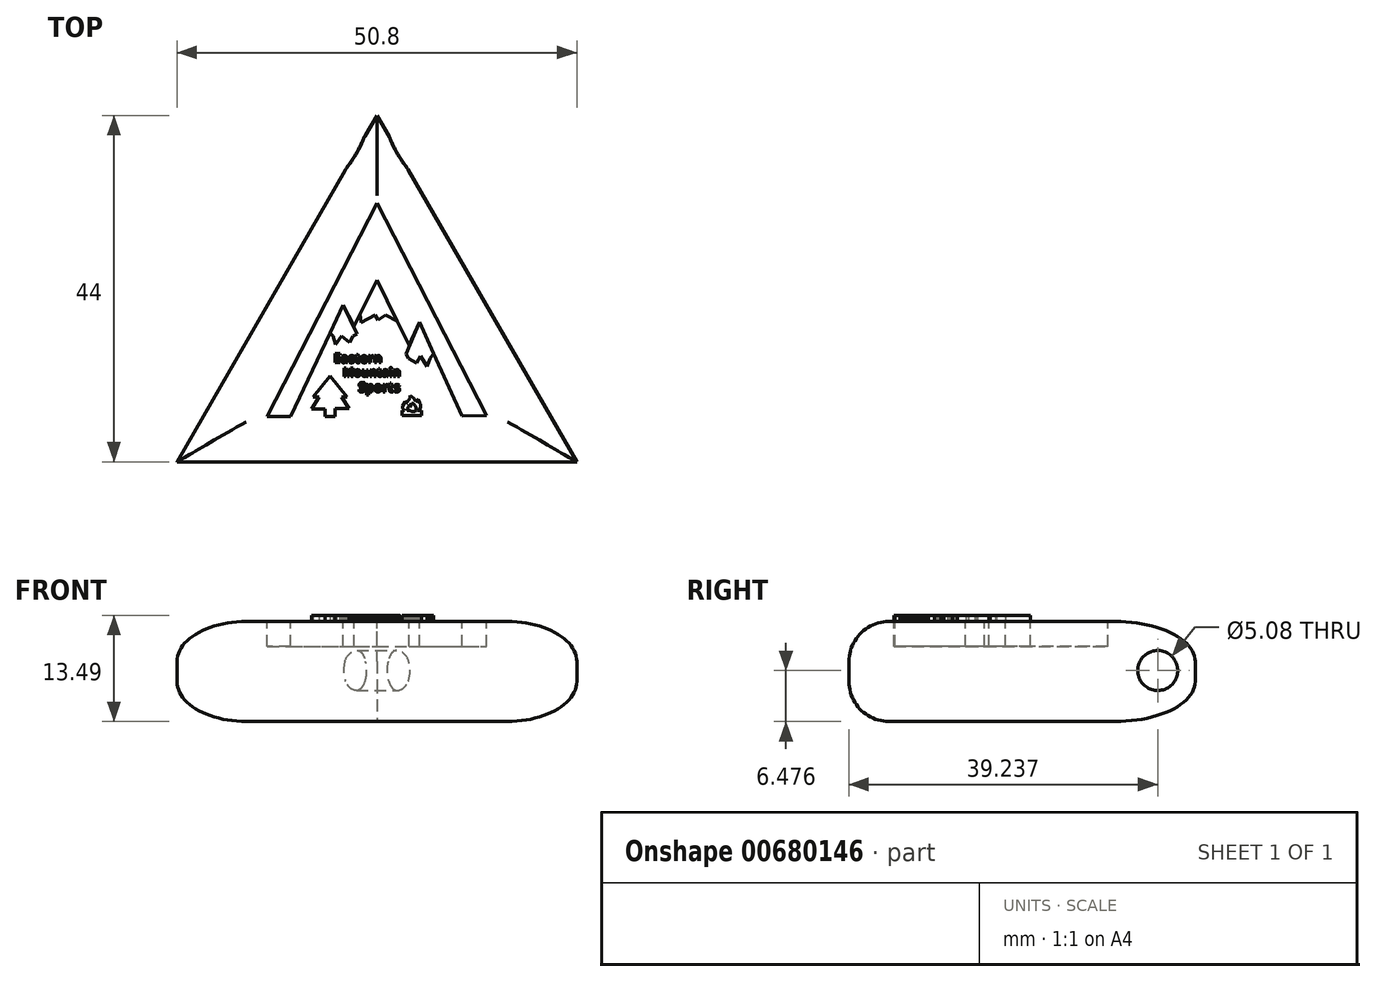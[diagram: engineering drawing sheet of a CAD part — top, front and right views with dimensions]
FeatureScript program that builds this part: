
annotation { "Feature Type Name" : "Feature", "Feature Type Description" : "" }
export const myFeature = defineFeature(function(context is Context, id is Id, definition is map)
    precondition{}
    {
        {
            var Q0;
            Q0=qCreatedBy(makeId("Top.planeOp"),FACE);
            var sketch = newSketch(context, id + "F0", { "sketchPlane" : qUnion([Q0])});
            skLineSegment(sketch, "E0", {"start": v(0, 54.4) * mm, "end": v(-25.4, 10.41) * mm});
            skLineSegment(sketch, "E1", {"start": v(-25.4, 10.41) * mm, "end": v(25.4, 10.41) * mm});
            skLineSegment(sketch, "E2", {"start": v(25.4, 10.41) * mm, "end": v(0, 54.4) * mm});
            skSolve(sketch);
        }
        {
            var Q0;
            Q0 = qSketchRegion(id + "F0", true);
            extrude(context, id + "F1", {"entities" : qUnion([Q0]), "depth" : 12.7 * mm, "offsetDistance" : 25.4 * mm});
        }
        {
            var Q0;
            Q0=makeQuery(id+"F1.opExtrude","CAP_EDGE",EDGE,{"disambiguationData":[OSD([sQuery(id+"F0.wireOp",EDGE,"E1")])],"isStart":false});
            var Q1;
            Q1=makeQuery(id+"F1.opExtrude","CAP_EDGE",EDGE,{"disambiguationData":[OSD([sQuery(id+"F0.wireOp",EDGE,"E0")])],"isStart":false});
            var Q2;
            Q2=makeQuery(id+"F1.opExtrude","CAP_EDGE",EDGE,{"disambiguationData":[OSD([sQuery(id+"F0.wireOp",EDGE,"E2")])],"isStart":false});
            var Q3;
            Q3=makeQuery(id+"F1.opExtrude","CAP_EDGE",EDGE,{"disambiguationData":[OSD([sQuery(id+"F0.wireOp",EDGE,"E1")])],"isStart":true});
            var Q4;
            Q4=makeQuery(id+"F1.opExtrude","CAP_EDGE",EDGE,{"disambiguationData":[OSD([sQuery(id+"F0.wireOp",EDGE,"E0")])],"isStart":true});
            var Q5;
            Q5=makeQuery(id+"F1.opExtrude","CAP_EDGE",EDGE,{"disambiguationData":[OSD([sQuery(id+"F0.wireOp",EDGE,"E2")])],"isStart":true});
            fillet(context, id + "F2", {"entities" : qUnion([Q0, Q1, Q2, Q3, Q4, Q5]), "radius" : 5.08 * mm, "tangentPropagation" : true, "allowEdgeOverflow" : false});
        }
        {
            var Q0;
            Q0=qCreatedBy(makeId("Right.planeOp"),FACE);
            var sketch = newSketch(context, id + "F3", { "sketchPlane" : qUnion([Q0])});
            skCircle(sketch, "E3", {"center": v(49.65, 6.48) * mm, "radius": 2.54 * mm});
            skSolve(sketch);
        }
        {
            var Q0;
            Q0 = qSketchRegion(id + "F3", true);
            extrude(context, id + "F4", {"entities" : qUnion([Q0]), "operationType" : NewBodyOperationType.REMOVE, "oppositeDirection" : true, "depth" : 25.4 * mm, "offsetDistance" : 25.4 * mm});
        }
        {
            var Q0;
            Q0 = qSketchRegion(id + "F3", true);
            extrude(context, id + "F5", {"entities" : qUnion([Q0]), "operationType" : NewBodyOperationType.REMOVE, "depth" : 25.4 * mm, "offsetDistance" : 25.4 * mm});
        }
        {
            var Q0;
            Q0=makeQuery(id+"F1.opExtrude","CAP_FACE",FACE,{"disambiguationData":[OSD([sQuery(id+"F0.wireOp",EDGE,"E0"),sQuery(id+"F0.wireOp",EDGE,"E1"),sQuery(id+"F0.wireOp",EDGE,"E2")])],"isStart":false});
            var sketch = newSketch(context, id + "F6", { "sketchPlane" : qUnion([Q0])});
            skLineSegment(sketch, "E4", {"start": v(-13.91, 16.14) * mm, "end": v(0, 43.3) * mm});
            skLineSegment(sketch, "E5", {"start": v(0, 43.3) * mm, "end": v(13.94, 16.26) * mm});
            skLineSegment(sketch, "E6", {"start": v(-10.95, 16.15) * mm, "end": v(-4.29, 30.3) * mm});
            skLineSegment(sketch, "E7", {"start": v(-4.29, 30.3) * mm, "end": v(-2.9, 27.63) * mm});
            skLineSegment(sketch, "E8", {"start": v(-2.9, 27.63) * mm, "end": v(0, 33.5) * mm});
            skLineSegment(sketch, "E9", {"start": v(0, 33.5) * mm, "end": v(4.07, 25.21) * mm});
            skLineSegment(sketch, "E10", {"start": v(4.07, 25.21) * mm, "end": v(5.4, 28.18) * mm});
            skLineSegment(sketch, "E11", {"start": v(5.4, 28.18) * mm, "end": v(10.85, 16.25) * mm});
            skLineSegment(sketch, "E12", {"start": v(-10.95, 16.15) * mm, "end": v(-13.91, 16.14) * mm});
            skLineSegment(sketch, "E13", {"start": v(10.85, 16.25) * mm, "end": v(13.94, 16.26) * mm});
            skLineSegment(sketch, "E14", {"start": v(-2.9, 27.63) * mm, "end": v(-2.47, 26.63) * mm});
            skSolve(sketch);
        }
        {
            var Q0;
            Q0 = qSketchRegion(id + "F6", true);
            extrude(context, id + "F7", {"entities" : qUnion([Q0]), "operationType" : NewBodyOperationType.REMOVE, "oppositeDirection" : true, "depth" : 3.17 * mm, "offsetDistance" : 25.4 * mm});
        }
        {
            var Q0;
            Q0=makeQuery(id+"F1.opExtrude","CAP_FACE",FACE,{"disambiguationData":[OSD([sQuery(id+"F0.wireOp",EDGE,"E0"),sQuery(id+"F0.wireOp",EDGE,"E1"),sQuery(id+"F0.wireOp",EDGE,"E2")])],"isStart":false});
            var sketch = newSketch(context, id + "F8", { "sketchPlane" : qUnion([Q0])});
            skLineSegment(sketch, "E15", {"start": v(-2.49, 26.64) * mm, "end": v(-3.03, 26.4) * mm});
            skLineSegment(sketch, "E16", {"start": v(-3.03, 26.4) * mm, "end": v(-3.48, 25.58) * mm});
            skLineSegment(sketch, "E17", {"start": v(-3.48, 25.58) * mm, "end": v(-4.5, 26.4) * mm});
            skLineSegment(sketch, "E18", {"start": v(-4.5, 26.4) * mm, "end": v(-5.27, 25.3) * mm});
            skLineSegment(sketch, "E19", {"start": v(-5.27, 25.3) * mm, "end": v(-5.55, 26.4) * mm});
            skLineSegment(sketch, "E20", {"start": v(-5.55, 26.4) * mm, "end": v(-5.96, 26.74) * mm});
            skLineSegment(sketch, "E21", {"start": v(-5.96, 26.74) * mm, "end": v(-4.29, 30.3) * mm});
            skLineSegment(sketch, "E22", {"start": v(-4.29, 30.3) * mm, "end": v(-2.49, 26.64) * mm});
            skLineSegment(sketch, "E23", {"start": v(-2, 28.13) * mm, "end": v(-2.13, 29.18) * mm});
            skLineSegment(sketch, "E24", {"start": v(-2.13, 29.18) * mm, "end": v(0, 33.5) * mm});
            skLineSegment(sketch, "E25", {"start": v(0, 33.5) * mm, "end": v(2.55, 28.31) * mm});
            skLineSegment(sketch, "E26", {"start": v(2.55, 28.31) * mm, "end": v(1.11, 29.03) * mm});
            skLineSegment(sketch, "E27", {"start": v(1.11, 29.03) * mm, "end": v(0.14, 28.44) * mm});
            skLineSegment(sketch, "E28", {"start": v(0.14, 28.44) * mm, "end": v(-0.22, 29.04) * mm});
            skLineSegment(sketch, "E29", {"start": v(-0.22, 29.04) * mm, "end": v(-2, 28.13) * mm});
            skLineSegment(sketch, "E30", {"start": v(3.7, 24.13) * mm, "end": v(4.04, 23.55) * mm});
            skLineSegment(sketch, "E31", {"start": v(4.04, 23.55) * mm, "end": v(5.04, 22.98) * mm});
            skLineSegment(sketch, "E32", {"start": v(5.04, 22.98) * mm, "end": v(5.54, 23.84) * mm});
            skLineSegment(sketch, "E33", {"start": v(5.54, 23.84) * mm, "end": v(6.35, 22.5) * mm});
            skLineSegment(sketch, "E34", {"start": v(6.35, 22.5) * mm, "end": v(6.78, 23.55) * mm});
            skLineSegment(sketch, "E35", {"start": v(6.78, 23.55) * mm, "end": v(7.23, 24.17) * mm});
            skLineSegment(sketch, "E36", {"start": v(7.23, 24.17) * mm, "end": v(5.4, 28.18) * mm});
            skLineSegment(sketch, "E37", {"start": v(5.4, 28.18) * mm, "end": v(3.7, 24.13) * mm});
            skLineSegment(sketch, "E38", {"start": v(-4.47, 18.65) * mm, "end": v(-3.54, 17.16) * mm});
            skLineSegment(sketch, "E39", {"start": v(-3.54, 17.16) * mm, "end": v(-5.28, 17.16) * mm});
            skLineSegment(sketch, "E40", {"start": v(-6.6, 17.15) * mm, "end": v(-8.32, 17.15) * mm});
            skLineSegment(sketch, "E41", {"start": v(-8.32, 17.15) * mm, "end": v(-7.32, 18.66) * mm});
            skLineSegment(sketch, "E42", {"start": v(-7.32, 18.66) * mm, "end": v(-8.09, 18.66) * mm});
            skLineSegment(sketch, "E43", {"start": v(-8.09, 18.66) * mm, "end": v(-5.96, 21.34) * mm});
            skLineSegment(sketch, "E44", {"start": v(-4.47, 18.65) * mm, "end": v(-3.76, 18.65) * mm});
            skLineSegment(sketch, "E45", {"start": v(-3.76, 18.65) * mm, "end": v(-5.96, 21.34) * mm});
            skLineSegment(sketch, "E46", {"start": v(-6.6, 17.15) * mm, "end": v(-6.6, 16.15) * mm});
            skLineSegment(sketch, "E47", {"start": v(-6.6, 16.15) * mm, "end": v(-5.28, 16.15) * mm});
            skLineSegment(sketch, "E48", {"start": v(-5.28, 16.15) * mm, "end": v(-5.28, 17.16) * mm});
            skText(sketch, "E49", { "text": "Eastern", "fontName": "OpenSans-Bold.ttf"});
            skText(sketch, "E50", { "text": "Mountain", "fontName": "OpenSans-Bold.ttf"});
            skText(sketch, "E51", { "text": "Sports", "fontName": "OpenSans-Bold.ttf"});
            skLineSegment(sketch, "E52.bottom", {"start": v(3.22, 16.26) * mm, "end": v(5.66, 16.26) * mm});
            skLineSegment(sketch, "E52.left", {"start": v(3.22, 16.26) * mm, "end": v(3.22, 16.9) * mm});
            skLineSegment(sketch, "E52.right", {"start": v(5.66, 16.26) * mm, "end": v(5.66, 16.9) * mm});
            skLineSegment(sketch, "E53", {"start": v(3.52, 16.9) * mm, "end": v(3.29, 17.2) * mm});
            skLineSegment(sketch, "E54", {"start": v(3.29, 17.2) * mm, "end": v(3.29, 17.52) * mm});
            skLineSegment(sketch, "E55", {"start": v(3.29, 17.52) * mm, "end": v(3.58, 18.04) * mm});
            skLineSegment(sketch, "E56", {"start": v(3.58, 18.04) * mm, "end": v(3.59, 18.16) * mm});
            skLineSegment(sketch, "E57", {"start": v(3.59, 18.16) * mm, "end": v(3.68, 18.06) * mm});
            skLineSegment(sketch, "E58", {"start": v(3.68, 18.06) * mm, "end": v(3.7, 17.85) * mm});
            skLineSegment(sketch, "E59", {"start": v(3.7, 17.85) * mm, "end": v(4.11, 18.3) * mm});
            skLineSegment(sketch, "E60", {"start": v(4.11, 18.3) * mm, "end": v(4.22, 18.53) * mm});
            skLineSegment(sketch, "E61", {"start": v(4.22, 18.53) * mm, "end": v(4.22, 18.83) * mm});
            skLineSegment(sketch, "E62", {"start": v(4.22, 18.83) * mm, "end": v(4.44, 18.7) * mm});
            skLineSegment(sketch, "E63", {"start": v(4.44, 18.7) * mm, "end": v(4.73, 18.45) * mm});
            skLineSegment(sketch, "E64", {"start": v(4.73, 18.45) * mm, "end": v(4.94, 18.05) * mm});
            skLineSegment(sketch, "E65", {"start": v(4.94, 18.05) * mm, "end": v(5.08, 18.13) * mm});
            skLineSegment(sketch, "E66", {"start": v(5.08, 18.13) * mm, "end": v(5.08, 18.38) * mm});
            skLineSegment(sketch, "E67", {"start": v(5.08, 18.38) * mm, "end": v(5.23, 18.25) * mm});
            skLineSegment(sketch, "E68", {"start": v(5.23, 18.25) * mm, "end": v(5.46, 17.95) * mm});
            skLineSegment(sketch, "E69", {"start": v(5.46, 17.95) * mm, "end": v(5.58, 17.76) * mm});
            skLineSegment(sketch, "E70", {"start": v(5.58, 17.76) * mm, "end": v(5.58, 17.48) * mm});
            skLineSegment(sketch, "E71", {"start": v(5.58, 17.48) * mm, "end": v(5.58, 17.35) * mm});
            skLineSegment(sketch, "E72", {"start": v(5.58, 17.35) * mm, "end": v(5.5, 17.16) * mm});
            skLineSegment(sketch, "E73", {"start": v(5.5, 17.16) * mm, "end": v(5.3, 16.98) * mm});
            skLineSegment(sketch, "E74", {"start": v(5.3, 16.98) * mm, "end": v(5.2, 16.9) * mm});
            skLineSegment(sketch, "E75", {"start": v(3.85, 16.9) * mm, "end": v(3.85, 17.12) * mm});
            skLineSegment(sketch, "E76", {"start": v(3.85, 17.12) * mm, "end": v(3.97, 17.34) * mm});
            skLineSegment(sketch, "E77", {"start": v(3.97, 17.34) * mm, "end": v(4.1, 17.5) * mm});
            skLineSegment(sketch, "E78", {"start": v(4.1, 17.5) * mm, "end": v(4.1, 17.68) * mm});
            skLineSegment(sketch, "E79", {"start": v(4.1, 17.68) * mm, "end": v(4.24, 17.62) * mm});
            skLineSegment(sketch, "E80", {"start": v(4.24, 17.62) * mm, "end": v(4.24, 17.4) * mm});
            skLineSegment(sketch, "E81", {"start": v(4.24, 17.4) * mm, "end": v(4.43, 17.62) * mm});
            skLineSegment(sketch, "E82", {"start": v(4.43, 17.62) * mm, "end": v(4.43, 17.9) * mm});
            skLineSegment(sketch, "E83", {"start": v(4.43, 17.9) * mm, "end": v(4.67, 17.77) * mm});
            skLineSegment(sketch, "E84", {"start": v(4.67, 17.77) * mm, "end": v(4.84, 17.53) * mm});
            skLineSegment(sketch, "E85", {"start": v(4.84, 17.53) * mm, "end": v(4.97, 17.34) * mm});
            skLineSegment(sketch, "E86", {"start": v(4.97, 17.34) * mm, "end": v(4.97, 17.13) * mm});
            skLineSegment(sketch, "E87", {"start": v(4.97, 17.13) * mm, "end": v(4.97, 16.9) * mm});
            skLineSegment(sketch, "E88", {"start": v(3.22, 16.9) * mm, "end": v(3.52, 16.9) * mm});
            skLineSegment(sketch, "E89", {"start": v(5.66, 16.9) * mm, "end": v(5.2, 16.9) * mm});
            skLineSegment(sketch, "E90", {"start": v(4.97, 16.9) * mm, "end": v(4.84, 16.8) * mm});
            skLineSegment(sketch, "E91", {"start": v(4.84, 16.8) * mm, "end": v(4.46, 16.78) * mm});
            skLineSegment(sketch, "E92", {"start": v(4.46, 16.78) * mm, "end": v(4.16, 16.9) * mm});
            skLineSegment(sketch, "E93", {"start": v(4.16, 16.9) * mm, "end": v(3.85, 16.9) * mm});
            const initialGuessF8  = {"E49": [-0.00548, 0.023, 1, 0, 0.00116], "E50": [-0.00432, 0.02127, 1, 0, 0.00108], "E51": [-0.00234, 0.0193, 1, 0, 0.0012]};
            skSetInitialGuess(sketch, initialGuessF8);
            skSolve(sketch);
        }
        {
            var Q0;
            Q0 = qSketchRegion(id + "F8", true);
            extrude(context, id + "F9", {"entities" : qUnion([Q0]), "operationType" : NewBodyOperationType.ADD, "depth" : 0.8 * mm, "offsetDistance" : 25.4 * mm});
        }
    });
